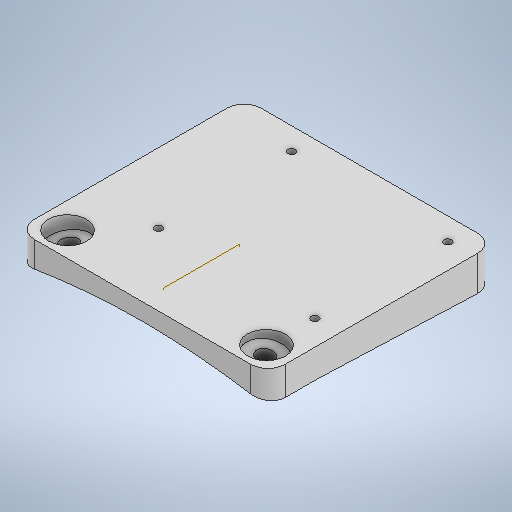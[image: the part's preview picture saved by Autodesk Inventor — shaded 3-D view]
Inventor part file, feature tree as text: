
AUTODESK INVENTOR PART (.ipt)
format: ipt  version: 2025 (Build 290162000, 162)  size: 428,032 bytes
history: native  units: in
note: dims shown in document units (in); Inventor stores cm internally (conversion verified against a paired STEP export)
features: sketch x8, extrude x7, mirror x2, other x2, revolve x1, plane x1, loft x1, fillet x1
ambient origin geometry x8: Origin, YZ Plane, XZ Plane, XY Plane, X Axis, Y Axis, Z Axis, Center Point
bodies: Solid1 (feature_tree)
feature tree (23):
  extrude  "Extrusion1"  Depth=0.25in
  revolve  "Revolution1"  [1 undecoded]
  extrude  "Extrusion2"  Depth=0.0563in
  plane  "Work Plane9"
  mirror  "Mirror1"
  extrude  "Extrusion3"  TaperAngle=90.0deg  [1 undecoded]
  mirror  "Mirror2"
  extrude  "Extrusion4"  TaperAngle=90.0deg  [1 undecoded]
  extrude  "Extrusion5"  Depth=0.6748in
  extrude  "Extrusion6"  TaperAngle=180.0deg  [1 undecoded]
  loft  "Loft1"
  extrude  "Extrusion7"  Depth=0.25in TaperAngle=0.0deg
  fillet  "Fillet1"  Radius=0.356in
  sketch  "Sketch1"  dims[d2=0.25in d3=1.5in]
  sketch  "Sketch2"  dims[d4=1.0in d5=0.0in d6=0.1in]
  sketch  "Sketch3"  dims[d7=0.12in d8=0.0563in]
  sketch  "Sketch5"  dims[d9=0.2in d10=90.0deg]
  sketch  "Sketch6"  dims[d11=0.275in d12=90.0deg]
  sketch  "Sketch7"  dims[d13=0.15in d14=0.6748in]
  sketch  "Sketch8"  dims[d15=0.1in d16=180.0deg]
  other  "Edges1"
  other  "Edges2"
  sketch  "Sketch9"  dims[d17=1.0in d18=0.0in d27=-1.8228in d28=1.0in d29=0.0in d30=0.356in d31=90.0deg d32=0.712in d33=1.0in d34=0.0in d52=2.585in d53=2.585in d54=0.36in d55=0.33in d56=0.11in d57=2.27in d58=1.93in d59=0.11in d60=0.11in d61=0.11in d62=0.2in d63=0.0in d64=0.345in d65=0.099in d66=0.099in d67=0.001in d68=0.0in d69=0.0in d70=90.0deg d71=0.0in d72=90.0deg d73=0.285in d74=0.0in d75=0.25in]
note: 4 required parameter values undecoded (feature->parameter linkage not recoverable at this tier; creation-order binding heuristic only, values carry confidence <= 0.55)